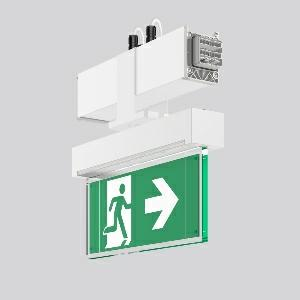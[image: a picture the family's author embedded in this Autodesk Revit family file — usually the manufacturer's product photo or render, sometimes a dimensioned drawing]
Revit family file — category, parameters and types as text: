
# Revit family: linedo_module_rz_9503rz_762_400_023_a273
name_source: partatom
category: Lighting Fixtures
units: mm (PartAtom-declared; Revit-internal decimal feet)

## family parameters
Cut with Voids When Loaded = No
Host = Face
Light Source = No
Part Type = Normal
Room Calculation Point = No
Round Connector Dimension = Use Diameter
Shared = No

## types (1)
- LINEDO Module RZ
    Apparent Load = 0 VA
    Default Elevation = 1800 mm
    Description = LINEDO, white, on/off
Continuous line luminaire, L 336 B 62 H 308, CBS, Stromkreis
    Height = 308 mm
    Lamp = 0 x
    Length = 336 mm
    Luminous efficacy = 0 lm/W
    Manufacturer = RZB
    ModVariant = No
    Model = 9503RZ.762.400.023
    Mounting Place = Ceiling
    Mounting Type = Surface mounted
    Number of Poles = 1
    OnlyDefault = Yes
    Power Factor = 1
    Product Name = LINEDO Module RZ
    Product group = Continuous line luminaire system Linedo IP 54
    ProductGroupID = 314
    Protection Class = Protection class I
    Protection Degree = IP 54
    RLX_Detail_Level = 1
    RLX_Emergency_Light_Flux = 0 lm
    RLX_Emergency_Type = 0
    RLX_Emergency_Type_DB = No
    RlxData = <blob elided: 33097 chars, md5=e6d5430a>
    Standby Power = 0 W
    System Light Flux = 0 lm
    System Power = 0 W
    Type Comments = Product without accessories
    Type Image = 9503rz.762.434.023.jpg
    URL = http://relux.com
    VarID = ---
    Voltage = 0 V
    Weight = 0.00 kg
    Width = 62 mm  [stored 0.203412 ft]

note: [stored X ft] marks values corroborated as IEEE doubles in the binary element streams (Revit-internal decimal feet)

## geometry (parser evidence)
native form markers: Blend x4, Sweep x12
no freeform markers — native parametric forms only
